# Revit family: Lighting-Floodlights-GEWISS-ESALITE-FL-LED_24K_DALI
name_source: partatom
category: Apparecchi per illuminazione
units: mm (PartAtom-declared; Revit-internal decimal feet)

## family parameters
Condiviso = No
Host = Superficie
Punto di calcolo locali = Sì
Quota connettore circolare = Usa diametro
Sorgente d'illuminazione = Sì
Taglio con vuoti quando caricato = No
Tipo di parte = Normale

## types (1)
- Lighting-Floodlights-GEWISS-ESALITE-FL-LED_24K_DALI
    Angolo inclinazione = -90.00°
    Application = Indoor / Outdoor
    Catalogue = LIGHTING
    Catalogue Range = ESALITE FL - 24K
    Colour = Grey RAL 9006
    Colour temperature: = 5700 K (CRI>80)
    Descrizione = ESALITE 24K ELL.5700K PRO+V.GR.DALI
    Driver type = Driver Led Dali
    Efficiency class of integrated LEDs = A ÷ A++
    Electrocod = 2444
    Emetti da lunghezza linea = 20 mm  [stored 0.0656168 ft]
    File diagramma fotometrico = GWS6455GD57K.IES
    Filtro dei colori = 16777215
    IDF = 1b9a74b8-16b9-46ee-a773-995bd203b2fc
    IDT = f7a9a771bf584c71b29cfc4a92707170
    IP degree = IP66
    Immagine tipo = ESALITE_FL.jpg
    Insulation class = I
    LED current. = 0,9A
    Lamp = LED - Not replaceable
    Life time L90B10 (Tq 25°C) = 100000H
    Life time L90B10 (Tq 50°C) = 44000H
    Lumen output (lm) = 22200
    Modello = GWS6455GD57K
    Nominal flux (lm) = 29000
    Numero poli = 1
    Operating temperature: = -30 +50 °C
    Optic = Elliptical
    Overvoltage resistance : = Common mode: 8KV; Differential mode: 6KV
    Potenza di sitema = Wxxx
    Produttore = GEWISS S.p.A.
    Prospetto di default = 1219 mm
    SEO = Floodlight
    STAFFA = <Per categoria>
    Shield type = Tempered glass
    Shock resistance = IK08
    System power = 210W
    Technical sheet = https://www.gewiss.com
    URL = https://www.gewiss.com
    V = 0 V
    Variazione temperatura colore lampada con luminosità attenuata = <Nessuno>
    Version file RFA = 20.11
    Versions = 5700K cold light
    Voltage = 220/240 V - 50/60 Hz
    Warranty = 5 years
    Weight (kg): = 13,7

note: [stored X ft] marks values corroborated as IEEE doubles in the binary element streams (Revit-internal decimal feet)

## geometry (parser evidence)
native form markers: Sweep x2
no freeform markers — native parametric forms only
